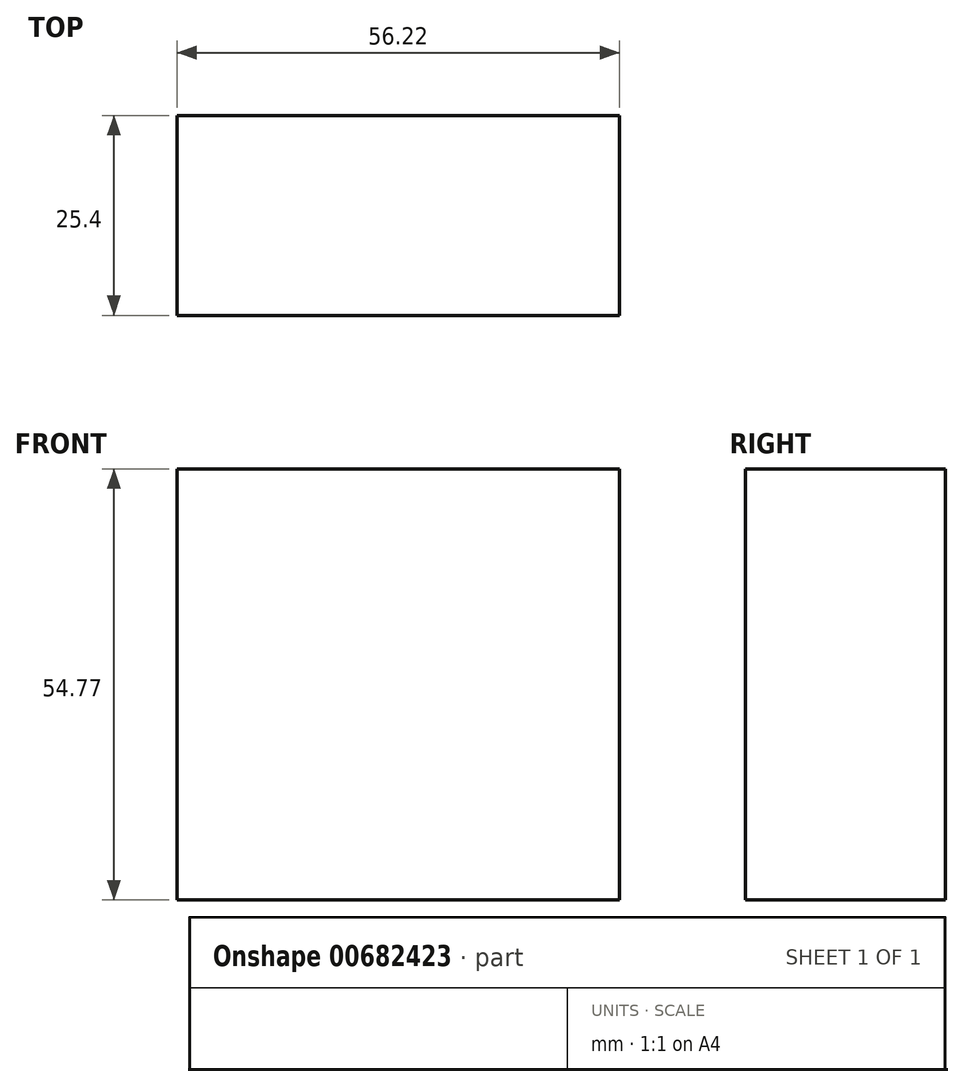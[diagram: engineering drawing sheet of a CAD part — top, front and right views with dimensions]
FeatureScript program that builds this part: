
annotation { "Feature Type Name" : "Feature", "Feature Type Description" : "" }
export const myFeature = defineFeature(function(context is Context, id is Id, definition is map)
    precondition{}
    {
        {
            var Q0;
            Q0=qCreatedBy(makeId("Front.planeOp"),FACE);
            var sketch = newSketch(context, id + "F0", { "sketchPlane" : qUnion([Q0])});
            skLineSegment(sketch, "E0", {"start": v(-56.22, 54.77) * mm, "end": v(-56.22, 0) * mm});
            skLineSegment(sketch, "E1", {"start": v(-56.22, 0) * mm, "end": v(0, 0) * mm});
            skLineSegment(sketch, "E2", {"start": v(-56.22, 54.77) * mm, "end": v(0, 54.77) * mm});
            skLineSegment(sketch, "E3", {"start": v(0, 54.77) * mm, "end": v(0, 0) * mm});
            skSolve(sketch);
        }
        {
            var Q0;
            Q0=makeQuery(id+"F0.imprint","IMPRINT",FACE,{"disambiguationData":[TD([[makeQuery(id+"F0.imprint","IMPRINT",EDGE,{"derivedFrom":sQuery(id+"F0.wireOp",EDGE,"E0")}),1.0]])]});
            var Q1;
            Q1 = qSketchRegion(id + "F0", true);
            extrude(context, id + "F1", {"entities" : qUnion([Q0, Q1]), "depth" : 25.4 * mm, "offsetDistance" : 25.4 * mm});
        }
    });
